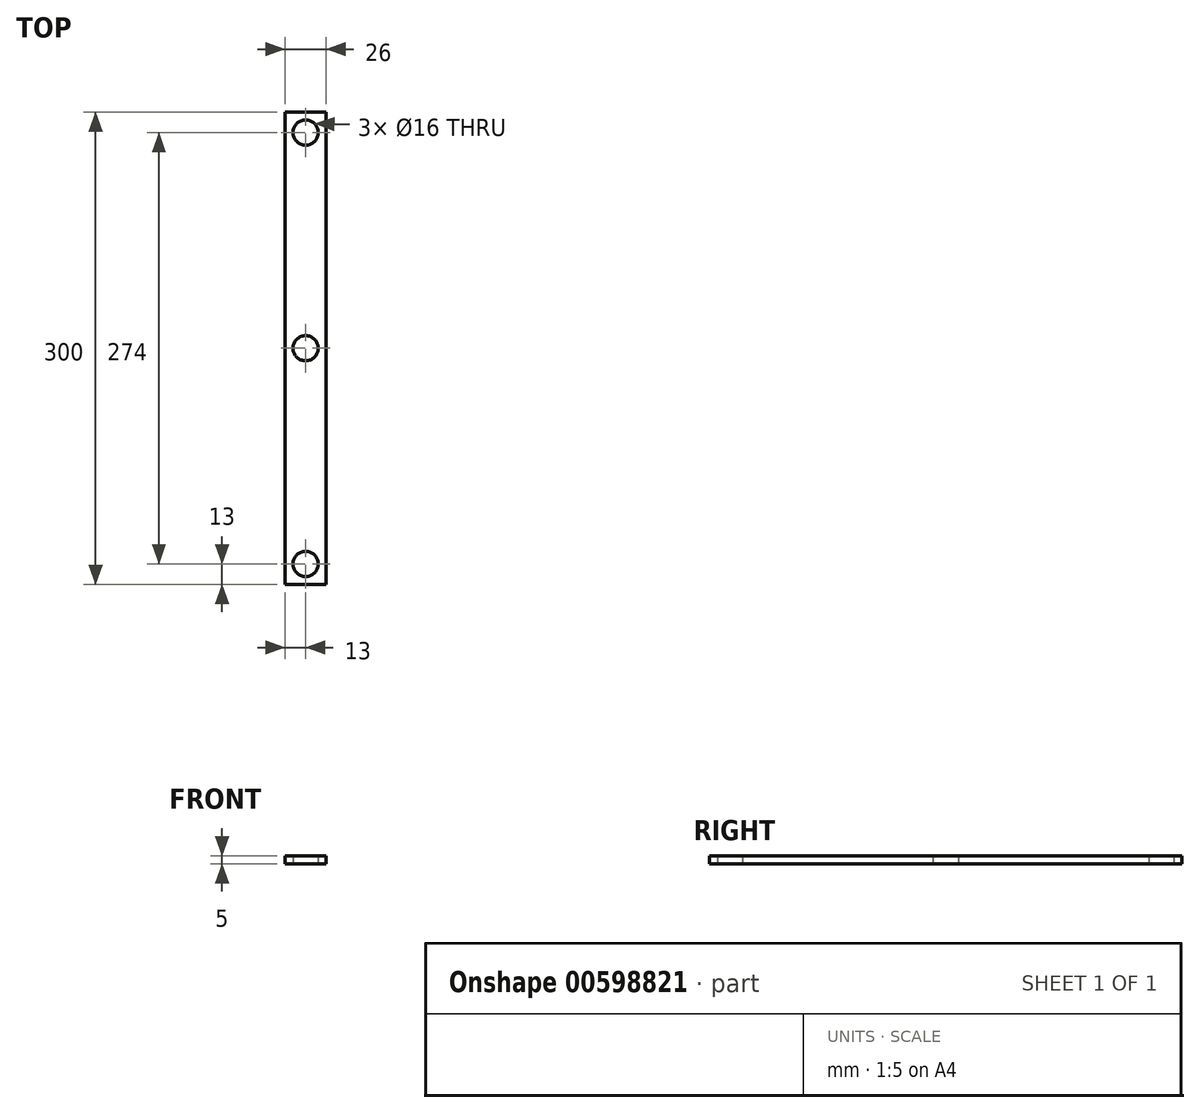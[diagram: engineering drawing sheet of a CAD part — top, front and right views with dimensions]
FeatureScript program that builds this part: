
annotation { "Feature Type Name" : "Feature", "Feature Type Description" : "" }
export const myFeature = defineFeature(function(context is Context, id is Id, definition is map)
    precondition{}
    {
        {
            var Q0;
            Q0=qCreatedBy(makeId("Top.planeOp"),FACE);
            var sketch = newSketch(context, id + "F0", { "sketchPlane" : qUnion([Q0])});
            skLineSegment(sketch, "E0.bottom", {"start": v(-13, 150) * mm, "end": v(13, 150) * mm});
            skLineSegment(sketch, "E0.top", {"start": v(-13, -150) * mm, "end": v(13, -150) * mm});
            skLineSegment(sketch, "E0.left", {"start": v(-13, 150) * mm, "end": v(-13, -150) * mm});
            skLineSegment(sketch, "E0.right", {"start": v(13, 150) * mm, "end": v(13, -150) * mm});
            skPoint(sketch, "E0.middle", {"position": v(0, 0) * mm});
            skCircle(sketch, "E1", {"center": v(0, 0) * mm, "radius": 8 * mm});
            skLineSegment(sketch, "E2", {"start": v(0, 150) * mm, "end": v(0, -150) * mm, "construction": true});
            skPoint(sketch, "E2.endSnap0", {"position": v(0, -150) * mm});
            skLineSegment(sketch, "E3.0", {"start": v(-13, 137) * mm, "end": v(13, 137) * mm, "construction": true});
            skLineSegment(sketch, "E4.0", {"start": v(-13, -137) * mm, "end": v(13, -137) * mm, "construction": true});
            skCircle(sketch, "E5", {"center": v(0, -137) * mm, "radius": 8 * mm});
            skCircle(sketch, "E6", {"center": v(0, 137) * mm, "radius": 8 * mm});
            skSolve(sketch);
        }
        {
            var Q0;
            Q0=makeQuery(id+"F0.imprint","IMPRINT",FACE,{"disambiguationData":[TD([[makeQuery(id+"F0.imprint","IMPRINT",EDGE,{"derivedFrom":sQuery(id+"F0.wireOp",EDGE,"E0.bottom")}),-1.0]])]});
            extrude(context, id + "F1", {"entities" : qUnion([Q0]), "depth" : 5 * mm, "offsetDistance" : 25 * mm});
        }
    });
